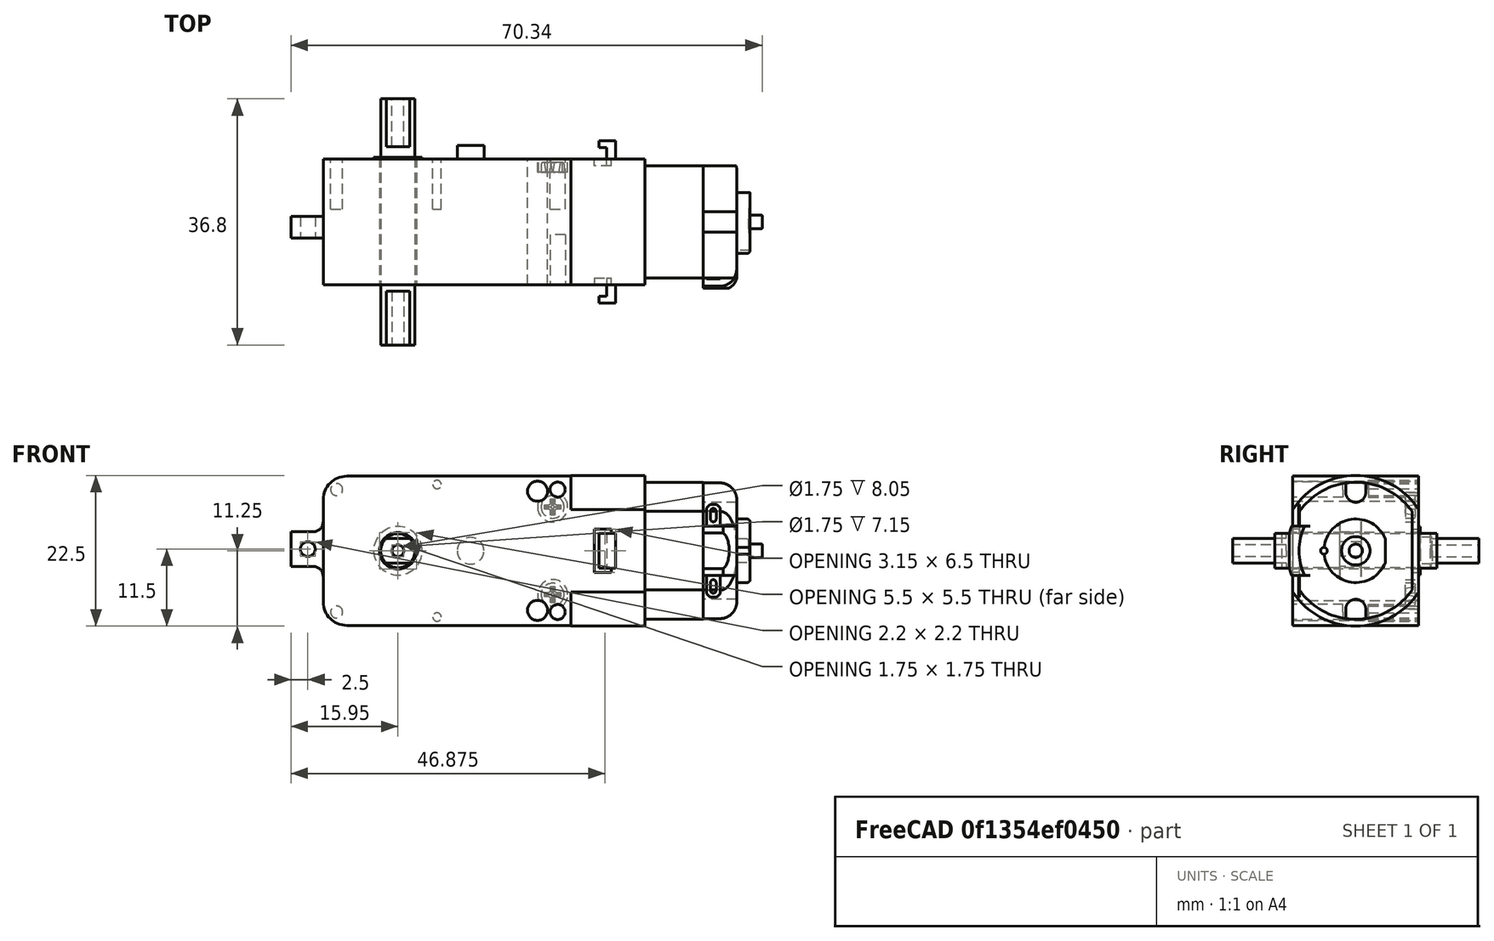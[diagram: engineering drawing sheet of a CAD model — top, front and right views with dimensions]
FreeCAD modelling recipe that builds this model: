
FCSTD DOCUMENT  (FreeCAD 0.21R33771 (Git))
Label: BO_motor
License: CERN Open Hardware Licence permissive
LicenseURL: https://cern-ohl.web.cern.ch/
objects: Part::FeaturePython×3, PartDesign::CoordinateSystem×2, Part::Box×2, Part::Cut×2, Part::Feature×1, App::Part×1, App::DocumentObjectGroup×1
note: 10 computed .brp shape members not serialized (recipe doc carries the construction recipe); baked Part::Feature solids carry a one-line shape summary decoded from their .brp

FEATURE [Part::Feature] Compound001  label="motoreducteur"
  Placement = pos=(25.85,-9.4,11.15) rot=(-1,0,0;1.5708rad)
  shape: bbox 70.34 x 38.2 x 22.5 mm, 234 faces, 3 solids (baked)
FEATURE [PartDesign::CoordinateSystem] Local_CS
  AttacherType = Attacher::AttachEngine3D
  AttachmentOffset = pos=(0,0,0) rot=(0,-1,0;1.5708rad)
  MapMode = 11
  Placement = pos=(-2.8e-15,-19.1,1.8e-15) rot=(0,0,-1;1.5708rad)
  Support = -> [Compound001]
FEATURE [PartDesign::CoordinateSystem] Local_CS001
  AttacherType = Attacher::AttachEngine3D
  AttachmentOffset = pos=(0,0,0) rot=(0,1,0;1.5708rad)
  MapMode = 11
  Placement = pos=(-2.8e-15,19.1,1.9e-15) rot=(0,0,1;4.71239rad)
  Support = -> [Compound001]
FEATURE [App::Part] Part
  Group = -> [Compound001,Local_CS,Local_CS001]
  Origin = -> Origin
  Placement = pos=(0,0,0) rot=(-0.57735,0.57735,-0.57735;4.18879rad)
FEATURE [Part::FeaturePython] Compound001_child0  label="motor_cap"  # WARN: FeaturePython — macro-defined, semantics opaque (R4)
  Base = -> Compound001
  FilterType = 1
  Invert = false
  OverrideMaxVal = 0
  WindowFrom = 80
  WindowTo = 100
  items = 0
FEATURE [Part::FeaturePython] Compound001_child1  label="motoreducteur.1"  # WARN: FeaturePython — macro-defined, semantics opaque (R4)
  Base = -> Compound001
  FilterType = 1
  Invert = false
  OverrideMaxVal = 0
  WindowFrom = 80
  WindowTo = 100
  items = 1
FEATURE [Part::FeaturePython] Compound001_child2  label="motor_body"  # WARN: FeaturePython — macro-defined, semantics opaque (R4)
  Base = -> Compound001
  FilterType = 1
  Invert = false
  OverrideMaxVal = 0
  WindowFrom = 80
  WindowTo = 100
  items = 2
FEATURE [Part::Box] Box  label="Cube"
  AttacherType = Attacher::AttachEngine3D
  Height = 10
  Length = 10
  Placement = pos=(-5,-28.4,-5) rot=(0,0,1;0rad)
  Width = 10
FEATURE [Part::Box] Box001  label="Cube001"
  AttacherType = Attacher::AttachEngine3D
  Height = 10
  Length = 10
  Placement = pos=(-5,18.4,-5) rot=(0,0,1;0rad)
  Width = 10
FEATURE [Part::Cut] Cut
  Base = -> Compound001_child1
  Tool = -> Box
FEATURE [Part::Cut] Cut001  label="motor_shaft"
  Base = -> Cut
  Refine = true
  Tool = -> Box001
FEATURE [App::DocumentObjectGroup] GrExplode_Compound001  label="Exploded motoreducteur"
  Group = -> [Compound001_child0,Compound001_child2,Cut001]
